# Revit family: Фильтр-грязевик 4111
name_source: partatom
category: Rohrzubehör
units: mm (PartAtom-declared; Revit-internal decimal feet)

## family parameters
Arbeitsebenenbasiert = Nein
Beim Laden mit Abzugskörper schneiden = Nein
Bemaßung runder Anschluss = Durchmesser verwenden
Gemeinsam genutzt = Nein
Immer vertikal = Ja
OmniClass-Nummer = 23.65.55.14
OmniClass-Titel = Valves for Liquid Services
Teiletyp = Unterbricht

## types (1)
- Фильтр-грязевик 4111
    Hersteller = HERZ Armaturen Ges.m.b.H.
    PN = 1600000.0 Pa
    SCRNCODE = 05;15;02
    SCRNSEQ = AWI;AWI_TYP="1011";2
    URL = www.herz-armaturen.ru
    Vorgabe-Ansicht = 0 mm  [stored 0 ft]
    W01 = 140.00°
    W02 = 45.00°
    Заглушка = Сталь St37
    Корпус = GG25
    Крепление фильтрующего элемента = Нержавеющая сталь
    Крышка = GG25
    Макс. рабочая температура = 120 °C
    Мин. рабочая температура = -10 °C
    Область применения = Применяются в системах тепло- и холодоснабжения.
    Среда = Качество теплоносителя в соответствии с ÖNORM H5195 и/или предписаниями VDI-Standard 2035.
Разрешается использование смеси этилен или пропиленгликоля в соотношении 25-50% с водой.
    Уплотнение заглушки = Медь
    Уплотнения = Klingerit
    Фильтрующий элемент (DN100-DN400) = AISI 304, размер ячейки 1500 мкм
    Фильтрующий элемент (DN50-DN80) = AISI 304, размер ячейки 600 мкм

note: [stored X ft] marks values corroborated as IEEE doubles in the binary element streams (Revit-internal decimal feet)
